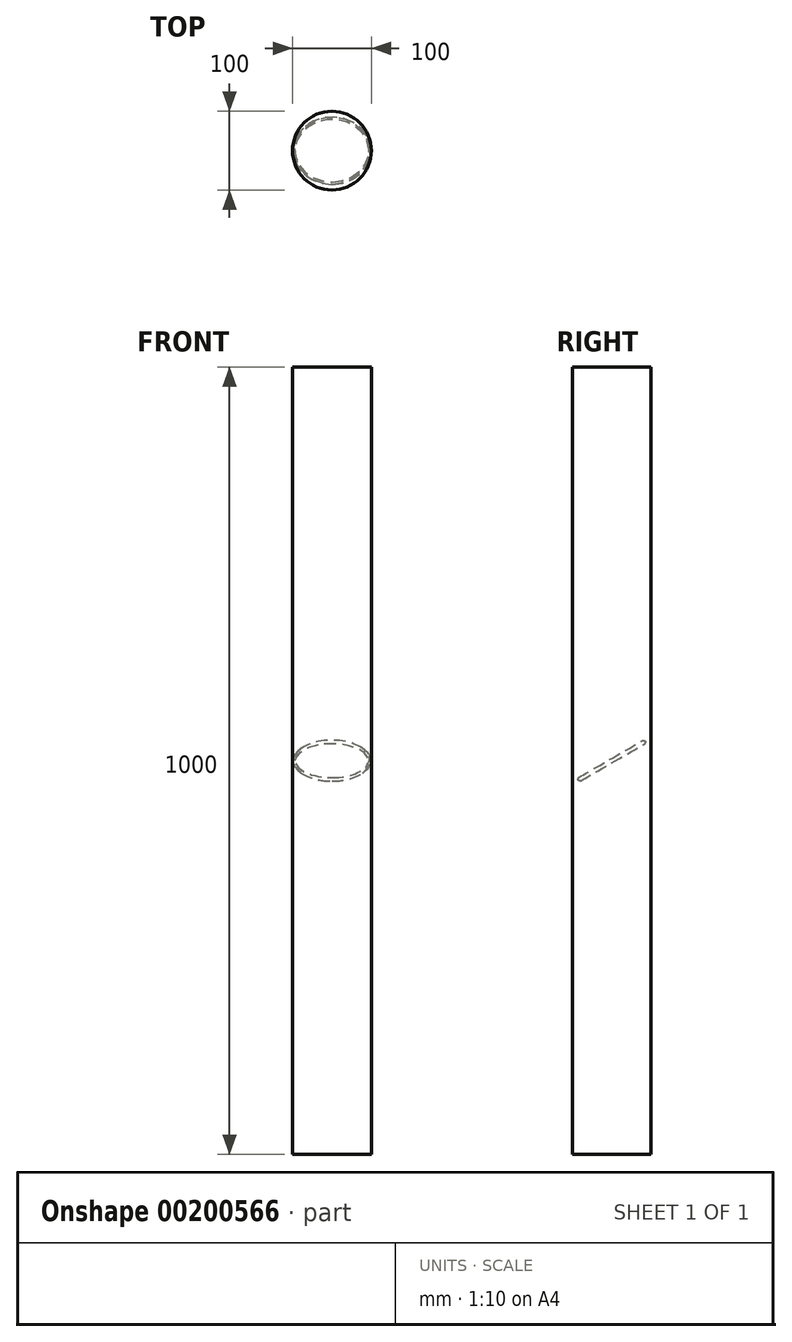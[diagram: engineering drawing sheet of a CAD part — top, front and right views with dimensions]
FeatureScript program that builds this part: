
annotation { "Feature Type Name" : "Feature", "Feature Type Description" : "" }
export const myFeature = defineFeature(function(context is Context, id is Id, definition is map)
    precondition{}
    {
        {
            var Q0;
            Q0=qCreatedBy(makeId("Top.planeOp"),FACE);
            var sketch = newSketch(context, id + "F0", { "sketchPlane" : qUnion([Q0])});
            skCircle(sketch, "E0", {"center": v(0, 0) * mm, "radius": 50 * mm});
            skSolve(sketch);
        }
        {
            var Q0;
            Q0=qSketchRegion(id+"F0",true);
            var Q1;
            Q1=sQuery(id+"F0.wireOp",EDGE,"E0");
            extrude(context, id + "F1", {"entities" : qUnion([Q0]), "surfaceEntities" : qUnion([Q1]), "endBound" : BoundingType.SYMMETRIC, "depth" : 5 * mm});
        }
        {
            var Q0;
            Q0=qCreatedBy(makeId("Top.planeOp"),FACE);
            var sketch = newSketch(context, id + "F2", { "sketchPlane" : qUnion([Q0])});
            skLineSegment(sketch, "E1", {"start": v(-75.72, 0) * mm, "end": v(75.22, 0) * mm});
            skSolve(sketch);
        }
        {
            var Q0;
            Q0=makeQuery(id+"F1.opExtrude","SWEPT_BODY",BODY,{"disambiguationData":[OSD([sQuery(id+"F0.wireOp",EDGE,"E0")])]});
            var Q1;
            Q1=sQuery(id+"F2.wireOp",EDGE,"E1");
            transform(context, id + "F3", {"entities" : qUnion([Q0]), "transformType" : TransformType.ROTATION, "transformAxis" : qUnion([Q1]), "angle" : 30 * degree, "makeCopy" : false});
        }
        {
            var Q0;
            Q0=makeQuery(id+"F1.opExtrude","CAP_EDGE",EDGE,{"disambiguationData":[OSD([sQuery(id+"F0.wireOp",EDGE,"E0")])],"isStart":false});
            var Q1;
            Q1=makeQuery(id+"F1.opExtrude","CAP_EDGE",EDGE,{"disambiguationData":[OSD([sQuery(id+"F0.wireOp",EDGE,"E0")])],"isStart":true});
            chamfer(context, id + "F4", {"entities" : qUnion([Q0, Q1]), "width" : 2.5 * mm, "tangentPropagation" : true});
        }
        {
            var Q0;
            {var subQ0=sQuery(id+"F0.wireOp",EDGE,"E0");Q0=makeQuery(id+"F4.opChamfer","BLEND_EDGE",EDGE,{"blendedFrom":[makeQuery(id+"F1.opExtrude","CAP_EDGE",EDGE,{"disambiguationData":[OSD([subQ0])],"isStart":true}),makeQuery(id+"F1.opExtrude","CAP_EDGE",EDGE,{"disambiguationData":[OSD([subQ0])],"isStart":false})],"blendedInto":[]});}
            fillet(context, id + "F5", {"entities" : qUnion([Q0]), "radius" : 2 * mm, "tangentPropagation" : true, "allowEdgeOverflow" : false});
        }
        {
            var Q0;
            Q0=makeQuery(id+"F0.imprint","IMPRINT",FACE,{"disambiguationData":[TD([[makeQuery(id+"F0.imprint","IMPRINT",EDGE,{"derivedFrom":sQuery(id+"F0.wireOp",EDGE,"E0")}),1.0]])]});
            extrude(context, id + "F6", {"entities" : qUnion([Q0]), "endBound" : BoundingType.SYMMETRIC, "depth" : 1000 * mm});
        }
    });
